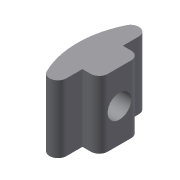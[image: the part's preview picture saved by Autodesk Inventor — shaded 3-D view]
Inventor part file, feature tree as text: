
AUTODESK INVENTOR PART (.ipt)
format: ipt  version: 2019.4 (Build 234330000, 330)  size: 155,136 bytes
history: native  units: mm
features: other x4, extrude x3, sketch x3, projected_geometry x2, mirror x1, fillet x1, plane x1, reference x1
ambient origin geometry x8: Origin, YZ Plane, XZ Plane, XY Plane, X Axis, Y Axis, Z Axis, Center Point
bodies: Solid1 (feature_tree)
feature tree (16):
  extrude  "Extrusion1"  Depth=2.0mm
  mirror  "Mirror1"
  fillet  "Fillet1"  Radius=4.5mm
  extrude  "Extrusion2"  Depth=8.0mm TaperAngle=0.0deg
  plane  "Work Plane1"
  extrude  "Extrusion3"  Depth=6.0mm
  sketch  "Sketch1"  dims[d0=2.4mm d1=2.0mm d2=4.5mm]
  sketch  "Sketch2"  dims[d3=0.5mm d4=8.0mm d5=0.0mm]
  projected_geometry  "Projected Loop1"
  sketch  "Sketch3"  dims[d6=1.0mm d7=2.8mm d8=8.0mm d9=0.0mm d10=-7.0mm d11=6.0mm d12=3.0mm d13=0.0mm d14=3.0mm]
  reference  "Reference1"
  projected_geometry  "Projected Loop2"
  other  "Assembly_neje_slide_y_wellplateholder_20mmrod.iam"
  other  "Application_Fluorescence_Microscope_Infinity_v3:1"
  other  "Assembly_Cube_Lens_holder_165mm_v3:2"
  other  "20_Cube_Insert_Lens_165mm:1"
